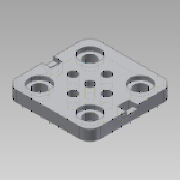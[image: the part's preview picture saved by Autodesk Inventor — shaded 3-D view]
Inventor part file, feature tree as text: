
AUTODESK INVENTOR PART (.ipt)
format: ipt  version: 2013 SP2 (Build 170200200, 200)  size: 181,248 bytes
history: native  units: mm
features: sketch x6, extrude x3, hole x3, fillet x1, plane x1, mirror x1
ambient origin geometry x8: Origin, YZ Plane, XZ Plane, XY Plane, X Axis, Y Axis, Z Axis, Center Point
bodies: Solid1 (feature_tree)
feature tree (15):
  extrude  "Extrusion1"  Depth=10.0mm
  hole  "Hole1"  [1 undecoded]
  hole  "Hole2"  [1 undecoded]
  sketch  "Sketch6"  dims[d16=15.0mm]
  hole  "Hole3"  [1 undecoded]
  fillet  "Fillet1"  Radius=2.5mm
  extrude  "Extrusion2"  Depth=5.25mm
  extrude  "Extrusion3"  Depth=6.7mm
  plane  "Work Plane1"
  mirror  "Mirror1"
  sketch  "Sketch1"  dims[d3=0.0mm d4=10.0mm]
  sketch  "Sketch2"  dims[d5=10.0mm d6=10.0mm]
  sketch  "Sketch4"  dims[d7=10.0mm]
  sketch  "Sketch5"  dims[d8=5.02mm d9=6.0mm d10=4.0mm d11=2.0mm d12=90.0deg d13=8.0mm d14=20.594885mm d15=15.0mm]
  sketch  "Sketch7"  dims[d17=7.14mm d18=6.0mm d19=12.0mm d20=2.18mm d21=90.0deg d22=6.35mm d23=0.0mm d24=6.17mm d25=2.5mm d27=5.25mm d28=6.7mm d29=6.35mm d30=0.0mm d31=2.18mm d33=6.35mm d34=0.0mm d35=31.9mm d36=5.0mm d37=6.0mm d38=10.1mm d39=2.0mm d40=90.0deg d41=8.0mm d42=20.594885mm]
note: 3 required parameter values undecoded (feature->parameter linkage not recoverable at this tier; creation-order binding heuristic only, values carry confidence <= 0.55)
